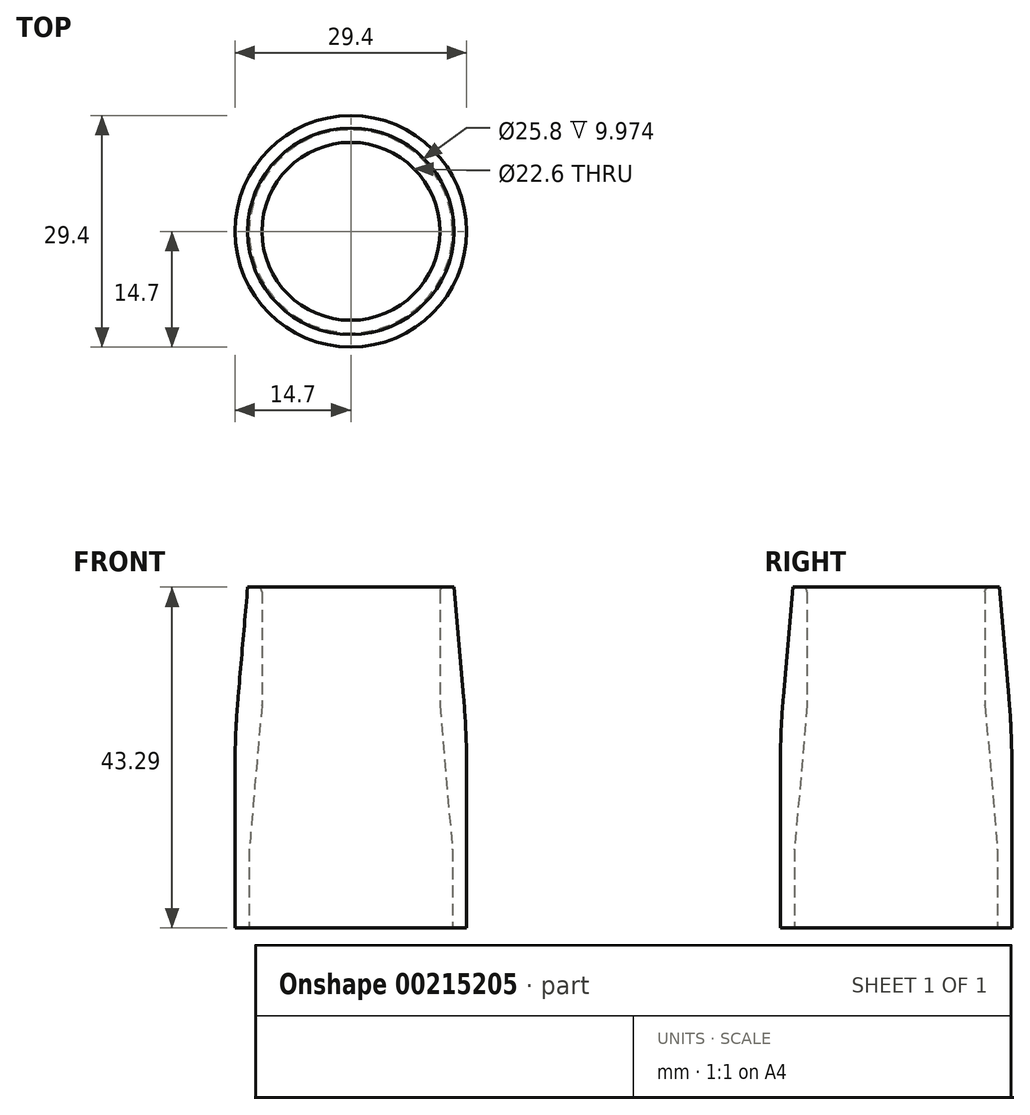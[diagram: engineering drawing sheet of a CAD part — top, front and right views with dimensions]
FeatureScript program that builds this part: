
annotation { "Feature Type Name" : "Feature", "Feature Type Description" : "" }
export const myFeature = defineFeature(function(context is Context, id is Id, definition is map)
    precondition{}
    {
        {
            var Q0;
            Q0=qCreatedBy(makeId("Front.planeOp"),FACE);
            var sketch = newSketch(context, id + "F0", { "sketchPlane" : qUnion([Q0])});
            skLineSegment(sketch, "E0", {"start": v(-14.7, 0) * mm, "end": v(-14.7, 15) * mm});
            skLineSegment(sketch, "E1", {"start": v(-13.1, 33.29) * mm, "end": v(-11.3, 33.29) * mm});
            skLineSegment(sketch, "E2", {"start": v(-11.3, 33.29) * mm, "end": v(-11.3, 18.29) * mm});
            skLineSegment(sketch, "E3", {"start": v(-14.7, 15) * mm, "end": v(-13.1, 33.29) * mm});
            skLineSegment(sketch, "E4", {"start": v(-12.9, 0) * mm, "end": v(-11.3, 18.29) * mm});
            skLineSegment(sketch, "E5", {"start": v(0, 0) * mm, "end": v(0, 33.29) * mm, "construction": true});
            skLineSegment(sketch, "E6", {"start": v(-14.7, 0) * mm, "end": v(-14.7, -10) * mm});
            skLineSegment(sketch, "E7", {"start": v(-14.7, -10) * mm, "end": v(-12.9, -10) * mm});
            skLineSegment(sketch, "E8", {"start": v(-12.9, -10) * mm, "end": v(-12.9, 0) * mm});
            skSolve(sketch);
        }
        {
            var Q0;
            Q0=makeQuery(id+"F0.imprint","IMPRINT",FACE,{"disambiguationData":[TD([[makeQuery(id+"F0.imprint","IMPRINT",EDGE,{"derivedFrom":sQuery(id+"F0.wireOp",EDGE,"E0")}),-1.0]])]});
            var Q1;
            Q1=sQuery(id+"F0.wireOp",EDGE,"E5");
            revolve(context, id + "F1", {"entities" : qUnion([Q0]), "axis" : qUnion([Q1]), "revolveType" : RevolveType.FULL});
        }
        {
            var Q0;
            Q0=makeQuery(id+"F1.opRevolve","SWEPT_EDGE",EDGE,{"disambiguationData":[OSD([sQuery(id+"F0.wireOp",EDGE,"ALipHEYh-1Etn-O9cB-F5IB-2im5ToMaoee3"),sQuery(id+"F0.wireOp",EDGE,"E4")])]});
            var Q1;
            Q1=makeQuery(id+"F1.opRevolve","SWEPT_EDGE",EDGE,{"disambiguationData":[OSD([sQuery(id+"F0.wireOp",EDGE,"E1"),sQuery(id+"F0.wireOp",EDGE,"E2")])]});
            fillet(context, id + "F2", {"entities" : qUnion([Q0, Q1]), "radius" : 0.6 * mm, "tangentPropagation" : true, "allowEdgeOverflow" : false});
        }
        {
            var Q0;
            Q0=makeQuery(id+"F1.opRevolve","SWEPT_EDGE",EDGE,{"disambiguationData":[OSD([sQuery(id+"F0.wireOp",EDGE,"E0"),sQuery(id+"F0.wireOp",EDGE,"E3")])]});
            fillet(context, id + "F3", {"entities" : qUnion([Q0]), "radius" : 100 * mm, "tangentPropagation" : true, "allowEdgeOverflow" : false});
        }
    });
